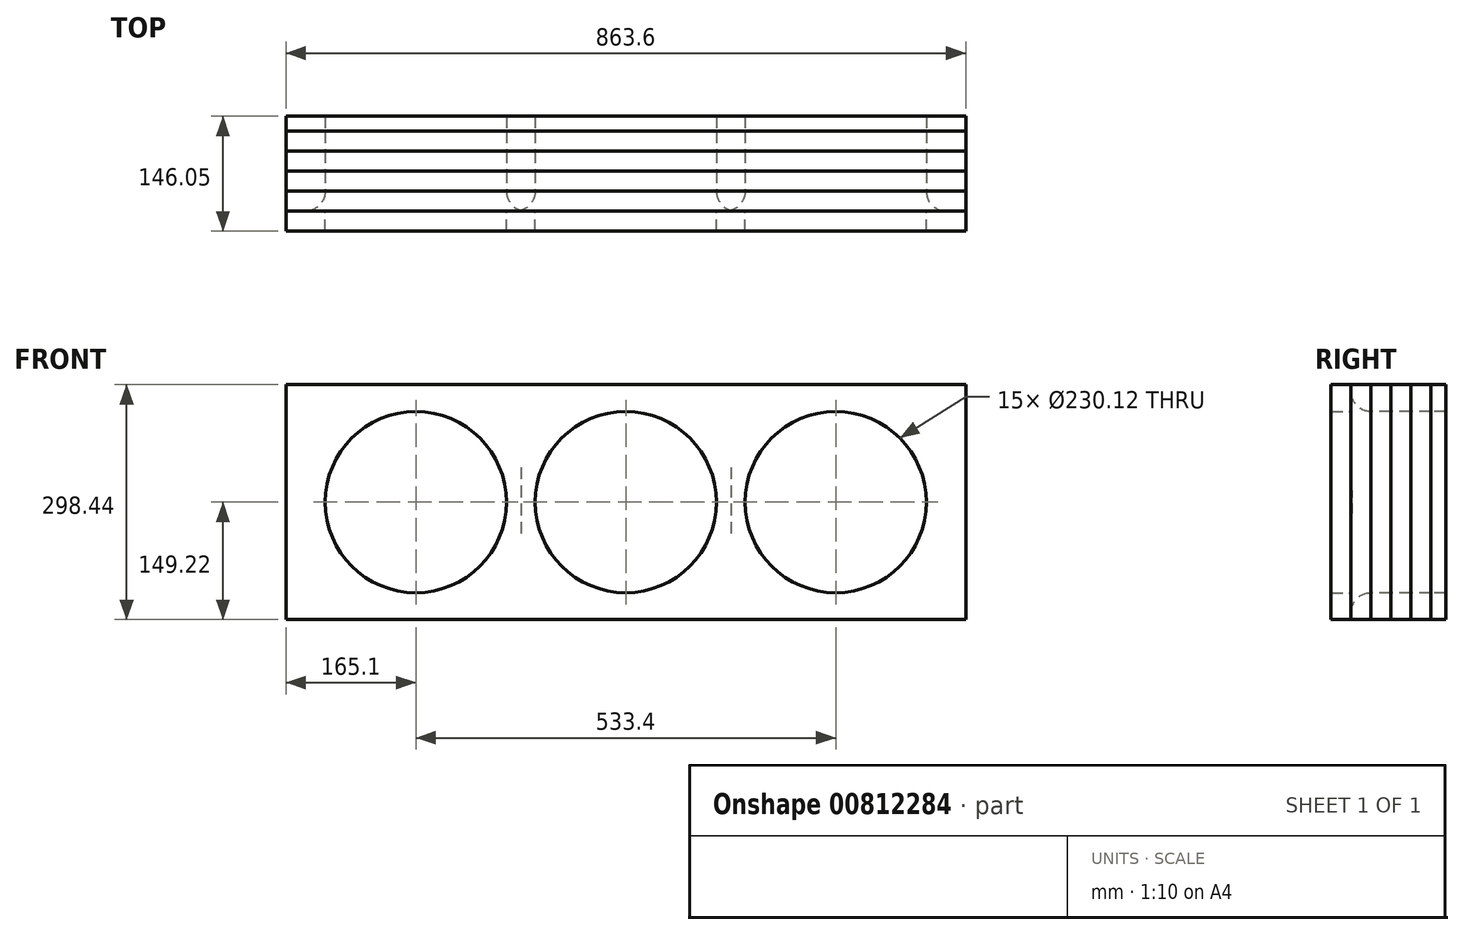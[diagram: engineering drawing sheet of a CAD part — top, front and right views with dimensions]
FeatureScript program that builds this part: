
annotation { "Feature Type Name" : "Feature", "Feature Type Description" : "" }
export const myFeature = defineFeature(function(context is Context, id is Id, definition is map)
    precondition{}
    {
        {
            var Q0;
            Q0=qCreatedBy(makeId("Front.planeOp"),FACE);
            var sketch = newSketch(context, id + "F0", { "sketchPlane" : qUnion([Q0])});
            skLineSegment(sketch, "E0.bottom", {"start": v(431.8, 149.23) * mm, "end": v(-431.8, 149.23) * mm});
            skLineSegment(sketch, "E0.top", {"start": v(431.8, -149.22) * mm, "end": v(-431.8, -149.22) * mm});
            skLineSegment(sketch, "E0.left", {"start": v(431.8, 149.23) * mm, "end": v(431.8, -149.23) * mm});
            skLineSegment(sketch, "E0.right", {"start": v(-431.8, 149.23) * mm, "end": v(-431.8, -149.22) * mm});
            skPoint(sketch, "E0.middle", {"position": v(0, 0) * mm});
            skCircle(sketch, "E1", {"center": v(0, 0) * mm, "radius": 115.06 * mm});
            skCircle(sketch, "E2", {"center": v(266.7, 0) * mm, "radius": 115.06 * mm});
            skCircle(sketch, "E3", {"center": v(-266.7, 0) * mm, "radius": 115.06 * mm});
            skSolve(sketch);
        }
        {
            var Q0;
            Q0=makeQuery(id+"F0.imprint","IMPRINT",FACE,{"disambiguationData":[TD([[makeQuery(id+"F0.imprint","IMPRINT",EDGE,{"derivedFrom":sQuery(id+"F0.wireOp",EDGE,"E0.bottom")}),1.0]])]});
            extrude(context, id + "F1", {"entities" : qUnion([Q0]), "depth" : 25.4 * mm, "offsetDistance" : 25.4 * mm});
        }
        {
            var Q0;
            Q0=makeQuery(id+"F1.opExtrude","CAP_FACE",FACE,{"disambiguationData":[OSD([sQuery(id+"F0.wireOp",EDGE,"E0.bottom"),sQuery(id+"F0.wireOp",EDGE,"E0.top"),sQuery(id+"F0.wireOp",EDGE,"E0.left"),sQuery(id+"F0.wireOp",EDGE,"E0.right"),sQuery(id+"F0.wireOp",EDGE,"E1"),sQuery(id+"F0.wireOp",EDGE,"E2"),sQuery(id+"F0.wireOp",EDGE,"E3")])],"isStart":true});
            extrude(context, id + "F2", {"entities" : qUnion([Q0]), "depth" : 25.4 * mm, "offsetDistance" : 25.4 * mm});
        }
        {
            var Q0;
            Q0=makeQuery(id+"F2.opExtrude","CAP_FACE",FACE,{"disambiguationData":[OSD([sQuery(id+"F0.wireOp",EDGE,"E0.bottom"),sQuery(id+"F0.wireOp",EDGE,"E0.top"),sQuery(id+"F0.wireOp",EDGE,"E0.left"),sQuery(id+"F0.wireOp",EDGE,"E0.right"),sQuery(id+"F0.wireOp",EDGE,"E1"),sQuery(id+"F0.wireOp",EDGE,"E2"),sQuery(id+"F0.wireOp",EDGE,"E3")])],"isStart":false});
            extrude(context, id + "F3", {"entities" : qUnion([Q0]), "depth" : 25.4 * mm, "offsetDistance" : 25.4 * mm});
        }
        {
            var Q0;
            Q0=makeQuery(id+"F3.opExtrude","CAP_FACE",FACE,{"disambiguationData":[OSD([sQuery(id+"F0.wireOp",EDGE,"E0.bottom"),sQuery(id+"F0.wireOp",EDGE,"E0.top"),sQuery(id+"F0.wireOp",EDGE,"E0.left"),sQuery(id+"F0.wireOp",EDGE,"E0.right"),sQuery(id+"F0.wireOp",EDGE,"E1"),sQuery(id+"F0.wireOp",EDGE,"E2"),sQuery(id+"F0.wireOp",EDGE,"E3")])],"isStart":false});
            extrude(context, id + "F4", {"entities" : qUnion([Q0]), "depth" : 25.4 * mm, "offsetDistance" : 25.4 * mm});
        }
        {
            var Q0;
            Q0=makeQuery(id+"F4.opExtrude","CAP_FACE",FACE,{"disambiguationData":[OSD([sQuery(id+"F0.wireOp",EDGE,"E0.bottom"),sQuery(id+"F0.wireOp",EDGE,"E0.top"),sQuery(id+"F0.wireOp",EDGE,"E0.left"),sQuery(id+"F0.wireOp",EDGE,"E0.right"),sQuery(id+"F0.wireOp",EDGE,"E1"),sQuery(id+"F0.wireOp",EDGE,"E2"),sQuery(id+"F0.wireOp",EDGE,"E3")])],"isStart":false});
            extrude(context, id + "F5", {"entities" : qUnion([Q0]), "depth" : 25.4 * mm, "offsetDistance" : 25.4 * mm});
        }
        {
            var Q0;
            Q0=makeQuery(id+"F5.opExtrude","CAP_FACE",FACE,{"disambiguationData":[OSD([sQuery(id+"F0.wireOp",EDGE,"E0.bottom"),sQuery(id+"F0.wireOp",EDGE,"E0.top"),sQuery(id+"F0.wireOp",EDGE,"E0.left"),sQuery(id+"F0.wireOp",EDGE,"E0.right"),sQuery(id+"F0.wireOp",EDGE,"E1"),sQuery(id+"F0.wireOp",EDGE,"E2"),sQuery(id+"F0.wireOp",EDGE,"E3")])],"isStart":false});
            extrude(context, id + "F6", {"entities" : qUnion([Q0]), "depth" : 19.05 * mm, "offsetDistance" : 25.4 * mm});
        }
        {
            var Q0;
            Q0=makeQuery(id+"F2.opExtrude","CAP_EDGE",EDGE,{"disambiguationData":[OSD([sQuery(id+"F0.wireOp",EDGE,"E3")])],"isStart":true});
            var Q1;
            Q1=makeQuery(id+"F2.opExtrude","CAP_EDGE",EDGE,{"disambiguationData":[OSD([sQuery(id+"F0.wireOp",EDGE,"E1")])],"isStart":true});
            var Q2;
            Q2=makeQuery(id+"F2.opExtrude","CAP_EDGE",EDGE,{"disambiguationData":[OSD([sQuery(id+"F0.wireOp",EDGE,"E2")])],"isStart":true});
            fillet(context, id + "F7", {"entities" : qUnion([Q0, Q1, Q2]), "radius" : 25.4 * mm, "allowEdgeOverflow" : false});
        }
    });
